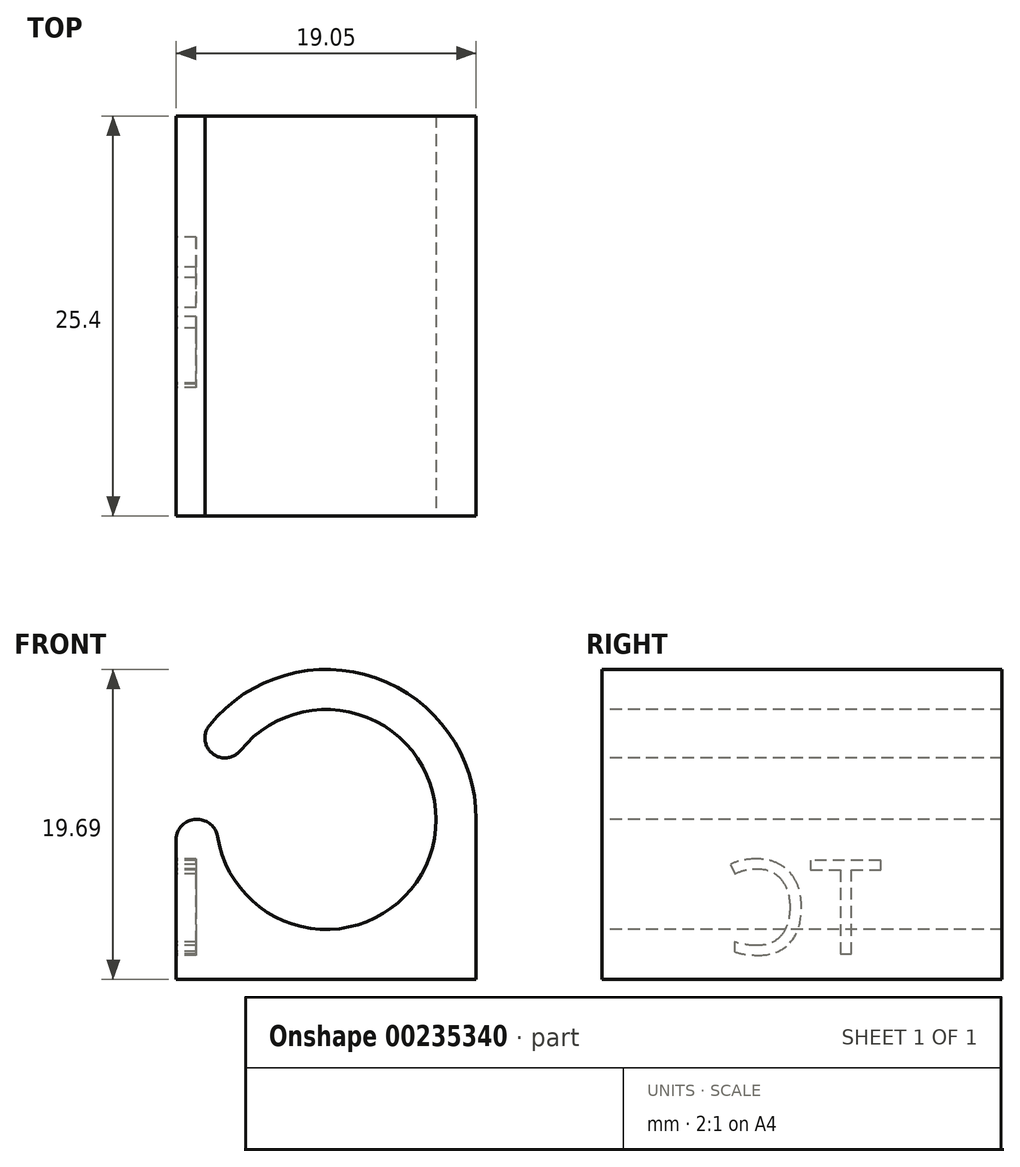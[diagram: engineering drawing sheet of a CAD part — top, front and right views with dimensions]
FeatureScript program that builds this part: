
annotation { "Feature Type Name" : "Feature", "Feature Type Description" : "" }
export const myFeature = defineFeature(function(context is Context, id is Id, definition is map)
    precondition{}
    {
        {
            var Q0;
            Q0=qCreatedBy(makeId("Top.planeOp"),FACE);
            var sketch = newSketch(context, id + "F0", { "sketchPlane" : qUnion([Q0])});
            skLineSegment(sketch, "E0.bottom", {"start": v(0, 0) * mm, "end": v(19.05, 0) * mm});
            skLineSegment(sketch, "E0.top", {"start": v(0, 25.4) * mm, "end": v(19.05, 25.4) * mm});
            skLineSegment(sketch, "E0.left", {"start": v(0, 0) * mm, "end": v(0, 25.4) * mm});
            skLineSegment(sketch, "E0.right", {"start": v(19.05, 0) * mm, "end": v(19.05, 25.4) * mm});
            skSolve(sketch);
        }
        {
            var Q0;
            Q0=qSketchRegion(id+"F0",true);
            extrude(context, id + "F1", {"entities" : qUnion([Q0]), "depth" : 3.17 * mm});
        }
        {
            var Q0;
            Q0=makeQuery(id+"F1.opExtrude","SWEPT_FACE",FACE,{"disambiguationData":[OSD([sQuery(id+"F0.wireOp",EDGE,"E0.bottom")])]});
            var sketch = newSketch(context, id + "F2", { "sketchPlane" : qUnion([Q0])});
            skLineSegment(sketch, "E1", {"start": v(19.05, 3.18) * mm, "end": v(19.05, 10.16) * mm});
            skArc(sketch, "E2", {"start": v(19.05, 10.16) * mm, "mid": v(12, 19.36) * mm, "end": v(1.28, 14.92) * mm});
            skLineSegment(sketch, "E3", {"start": v(1.28, 14.92) * mm, "end": v(3.48, 13.65) * mm});
            skArc(sketch, "E4", {"start": v(2.54, 10.16) * mm, "mid": v(16.27, 8.35) * mm, "end": v(3.48, 13.65) * mm});
            skLineSegment(sketch, "E5", {"start": v(9.53, 3.18) * mm, "end": v(9.53, 10.16) * mm, "construction": true});
            skLineSegment(sketch, "E6", {"start": v(9.53, 10.16) * mm, "end": v(1.28, 14.92) * mm, "construction": true});
            skLineSegment(sketch, "E7", {"start": v(0, 10.16) * mm, "end": v(0, 3.18) * mm});
            skLineSegment(sketch, "E8", {"start": v(0, 3.18) * mm, "end": v(19.05, 3.18) * mm});
            skLineSegment(sketch, "E9", {"start": v(2.54, 10.16) * mm, "end": v(0, 10.16) * mm});
            skLineSegment(sketch, "E10", {"start": v(9.52, 10.16) * mm, "end": v(0, 10.16) * mm, "construction": true});
            skSolve(sketch);
        }
        {
            var Q0;
            Q0=qSketchRegion(id+"F2",true);
            var Q1;
            Q1=makeQuery(id+"F1.opExtrude","SWEPT_FACE",FACE,{"disambiguationData":[OSD([sQuery(id+"F0.wireOp",EDGE,"E0.top")])]});
            extrude(context, id + "F3", {"entities" : qUnion([Q0]), "operationType" : NewBodyOperationType.ADD, "endBound" : BoundingType.UP_TO_SURFACE, "oppositeDirection" : true, "endBoundEntityFace" : qUnion([Q1]), "depth" : 25.4 * mm});
        }
        {
            var Q0;
            Q0=makeQuery(id+"F3.opExtrude","SWEPT_EDGE",EDGE,{"disambiguationData":[OSD([sQuery(id+"F2.wireOp",EDGE,"E2"),sQuery(id+"F2.wireOp",EDGE,"E3")])]});
            var Q1;
            Q1=makeQuery(id+"F3.opExtrude","SWEPT_EDGE",EDGE,{"disambiguationData":[OSD([sQuery(id+"F2.wireOp",EDGE,"E3"),sQuery(id+"F2.wireOp",EDGE,"E4")])]});
            var Q2;
            Q2=makeQuery(id+"F3.opExtrude","SWEPT_EDGE",EDGE,{"disambiguationData":[OSD([sQuery(id+"F2.wireOp",EDGE,"E4"),sQuery(id+"F2.wireOp",EDGE,"E9")])]});
            var Q3;
            Q3=makeQuery(id+"F3.opExtrude","SWEPT_EDGE",EDGE,{"disambiguationData":[OSD([sQuery(id+"F2.wireOp",EDGE,"E7"),sQuery(id+"F2.wireOp",EDGE,"E9")])]});
            fillet(context, id + "F4", {"entities" : qUnion([Q0, Q1, Q2, Q3]), "radius" : 1.27 * mm, "tangentPropagation" : true, "allowEdgeOverflow" : false});
        }
        {
            var Q0;
            Q0=makeQuery(id+"F1.opExtrude","CAP_FACE",FACE,{"disambiguationData":[OSD([sQuery(id+"F0.wireOp",EDGE,"E0.bottom"),sQuery(id+"F0.wireOp",EDGE,"E0.top"),sQuery(id+"F0.wireOp",EDGE,"E0.left"),sQuery(id+"F0.wireOp",EDGE,"E0.right")])],"isStart":true});
            var sketch = newSketch(context, id + "F5", { "sketchPlane" : qUnion([Q0])});
            skLineSegment(sketch, "E11.bottom", {"start": v(19.05, -6.35) * mm, "end": v(6.35, -6.35) * mm});
            skLineSegment(sketch, "E11.top", {"start": v(19.05, -19.05) * mm, "end": v(6.35, -19.05) * mm});
            skLineSegment(sketch, "E11.left", {"start": v(19.05, -6.35) * mm, "end": v(19.05, -19.05) * mm});
            skLineSegment(sketch, "E11.right", {"start": v(6.35, -6.35) * mm, "end": v(6.35, -19.05) * mm});
            skLineSegment(sketch, "E12", {"start": v(6.35, -19.05) * mm, "end": v(19.05, -25.4) * mm, "construction": true});
            skLineSegment(sketch, "E13", {"start": v(6.35, -6.35) * mm, "end": v(19.05, 0) * mm, "construction": true});
            skSolve(sketch);
        }
        {
            var Q0;
            Q0=makeQuery(id+"F3.boolean.opBoolean","MERGE",FACE,{"derivedFrom":[makeQuery(id+"F1.opExtrude","SWEPT_FACE",FACE,{"disambiguationData":[OSD([sQuery(id+"F0.wireOp",EDGE,"E0.left")])]}),makeQuery(id+"F3.opExtrude","SWEPT_FACE",FACE,{"disambiguationData":[OSD([sQuery(id+"F2.wireOp",EDGE,"E7")])]})]});
            var sketch = newSketch(context, id + "F6", { "sketchPlane" : qUnion([Q0])});
            skText(sketch, "E14", { "text": "TC", "fontName": "OpenSans-Regular.ttf"});
            skLineSegment(sketch, "E15", {"start": v(-17.78, 1.62) * mm, "end": v(-25.4, 0) * mm, "construction": true});
            skLineSegment(sketch, "E16", {"start": v(-7.62, 1.62) * mm, "end": v(0, 0) * mm, "construction": true});
            const initialGuessF6  = {"E14": [-0.01778, 0.00162, 1, 0, 0.006]};
            skSetInitialGuess(sketch, initialGuessF6);
            skSolve(sketch);
        }
        {
            var Q0;
            Q0=qSketchRegion(id+"F6",true);
            extrude(context, id + "F7", {"entities" : qUnion([Q0]), "operationType" : NewBodyOperationType.REMOVE, "oppositeDirection" : true, "depth" : 1.27 * mm});
        }
    });
